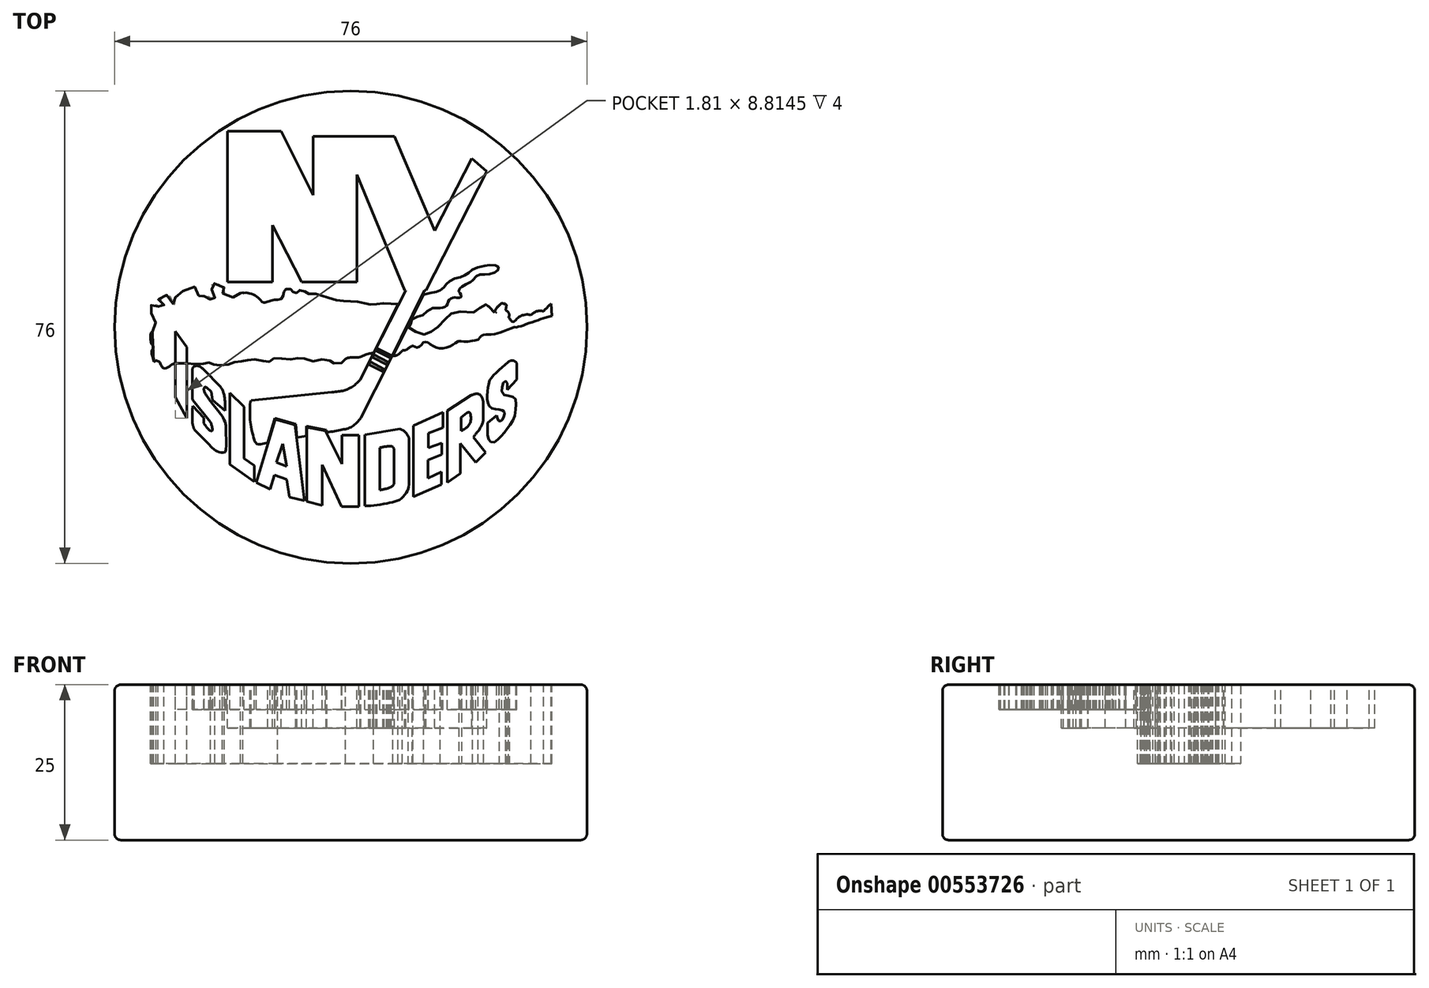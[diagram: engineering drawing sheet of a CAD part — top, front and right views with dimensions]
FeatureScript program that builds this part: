
annotation { "Feature Type Name" : "Feature", "Feature Type Description" : "" }
export const myFeature = defineFeature(function(context is Context, id is Id, definition is map)
    precondition{}
    {
        {
            var Q0;
            Q0=qCreatedBy(makeId("Top.planeOp"),FACE);
            var sketch = newSketch(context, id + "F0", { "sketchPlane" : qUnion([Q0])});
            skCircle(sketch, "E0", {"center": v(0, -1.1) * mm, "radius": 38 * mm});
            skLineSegment(sketch, "E1", {"start": v(0, 69.03) * mm, "end": v(0, -71.76) * mm, "construction": true});
            skLineSegment(sketch, "E2", {"start": v(-75.61, 0) * mm, "end": v(99.67, 0) * mm, "construction": true});
            skSolve(sketch);
        }
        {
            var Q0;
            Q0 = qSketchRegion(id + "F0", true);
            extrude(context, id + "F1", {"entities" : qUnion([Q0]), "depth" : 25 * mm, "offsetDistance" : 25 * mm});
        }
        {
            var Q0;
            Q0=makeQuery(id+"F1.opExtrude","CAP_FACE",FACE,{"disambiguationData":[OSD([sQuery(id+"F0.wireOp",EDGE,"E0")])],"isStart":false});
            var sketch = newSketch(context, id + "F2", { "sketchPlane" : qUnion([Q0])});
            skLineSegment(sketch, "E3", {"start": v(-35.12, 0) * mm, "end": v(34.88, 0) * mm, "construction": true});
            skLineSegment(sketch, "E4", {"start": v(-0.12, 35) * mm, "end": v(-0.12, -35) * mm, "construction": true});
            skFitSpline(sketch, "E5", {"points": [v(11.7, 4.15) * mm, v(12.74, 4.37) * mm, v(13.63, 4.59) * mm, v(14.2, 4.75) * mm, v(14.49, 4.87) * mm, v(14.91, 5.19) * mm, v(15.25, 5.66) * mm, v(15.5, 5.95) * mm, v(15.74, 6.16) * mm, v(16.14, 6.45) * mm, v(17.03, 6.84) * mm, v(17.65, 6.97) * mm, v(18.13, 7.13) * mm, v(18.63, 7.48) * mm, v(19.04, 7.7) * mm, v(19.46, 8.1) * mm, v(19.77, 8.33) * mm, v(21.3, 8.7) * mm, v(21.78, 8.8) * mm, v(22.45, 8.88) * mm, v(23.2, 8.86) * mm, v(23.6, 8.72) * mm, v(23.78, 8.58) * mm, v(23.82, 8.4) * mm, v(23.7, 8.11) * mm, v(23.48, 7.92) * mm, v(23.04, 7.63) * mm, v(22.45, 7.44) * mm, v(21.78, 7.39) * mm, v(21.36, 7.4) * mm, v(20.84, 7.4) * mm, v(20.5, 7.28) * mm, v(20.19, 7.05) * mm, v(19.63, 6.42) * mm], "startDerivative": vector(24.71, 4.93) * mm, "endDerivative": vector(-15.7, -18.75) * mm});
            skFitSpline(sketch, "E6", {"points": [v(19.63, 6.42) * mm, v(19.32, 6.22) * mm, v(18.96, 6.04) * mm, v(18.65, 5.87) * mm, v(18.35, 5.71) * mm, v(18.1, 5.56) * mm, v(17.82, 5.35) * mm, v(17.6, 5.17) * mm, v(17.5, 5.01) * mm, v(17.42, 4.92) * mm, v(17.36, 4.73) * mm, v(17.38, 4.6) * mm, v(17.62, 4.34) * mm, v(17.77, 4.07) * mm, v(17.79, 3.85) * mm, v(17.66, 3.7) * mm, v(17.42, 3.62) * mm, v(17.09, 3.65) * mm, v(16.9, 3.71) * mm, v(16.72, 3.72) * mm, v(16.47, 3.67) * mm, v(16.23, 3.58) * mm, v(16.09, 3.5) * mm, v(15.85, 3.3) * mm, v(15.7, 3.1) * mm, v(15.64, 2.87) * mm, v(15.55, 2.58) * mm, v(15.44, 2.41) * mm, v(15.27, 2.24) * mm, v(15.04, 2.12) * mm, v(14.7, 2.01) * mm, v(14.41, 2) * mm], "startDerivative": vector(-7.8, -5.36) * mm, "endDerivative": vector(-8.37, 0.32) * mm});
            skFitSpline(sketch, "E7", {"points": [v(14.41, 2) * mm, v(13.84, 2) * mm, v(13.39, 2) * mm, v(13.15, 1.97) * mm, v(12.9, 1.87) * mm, v(12.56, 1.72) * mm, v(12.29, 1.49) * mm, v(12.05, 1.25) * mm, v(11.85, 1) * mm, v(11.68, 0.85) * mm, v(11.52, 0.74) * mm, v(11.27, 0.7) * mm, v(10.98, 0.66) * mm, v(10.63, 0.6) * mm, v(10.3, 0.47) * mm, v(10.03, 0.34) * mm, v(9.87, 0.2) * mm, v(9.82, -0.1) * mm, v(9.85, -0.3) * mm, v(9.7, -0.57) * mm, v(9.56, -0.74) * mm, v(9.37, -0.82) * mm, v(9.23, -0.85) * mm, v(9.16, -0.94) * mm, v(9.27, -1.08) * mm, v(9.63, -1.38) * mm, v(10.17, -1.66) * mm, v(10.63, -1.9) * mm, v(11.32, -2.17) * mm, v(11.8, -2.26) * mm, v(12.26, -2.18) * mm, v(12.67, -2) * mm, v(13.18, -1.71) * mm, v(13.63, -1.38) * mm, v(14, -1.08) * mm, v(14.58, -0.5) * mm, v(15.24, 0.2) * mm, v(15.7, 0.68) * mm, v(16, 0.98) * mm, v(16.33, 1.22) * mm, v(16.62, 1.37) * mm, v(18.1, 1.38) * mm, v(19.53, 1.32) * mm, v(20.02, 1.3) * mm, v(20.4, 1.61) * mm, v(20.8, 2.01) * mm, v(21.28, 2.45) * mm, v(21.53, 2.55) * mm, v(21.76, 2.58) * mm, v(22.07, 2.5) * mm, v(22.26, 2.41) * mm, v(22.37, 2.2) * mm, v(22.5, 1.9) * mm, v(22.65, 1.62) * mm, v(22.78, 1.48) * mm, v(23.09, 1.31) * mm, v(23.33, 1.26) * mm, v(23.42, 1.48) * mm, v(23.48, 2.06) * mm, v(23.73, 2.46) * mm, v(24.06, 2.7) * mm, v(24.43, 2.83) * mm, v(24.7, 2.89) * mm, v(24.9, 2.76) * mm, v(25.02, 2.58) * mm, v(25.01, 2.18) * mm, v(24.98, 1.94) * mm, v(24.9, 1.74) * mm, v(24.94, 1.64) * mm], "startDerivative": vector(-31.94, -0.17) * mm, "endDerivative": vector(9.21, -12.06) * mm});
            skFitSpline(sketch, "E8", {"points": [v(24.94, 1.64) * mm, v(25.2, 1.45) * mm, v(25.4, 1.24) * mm, v(25.52, 0.97) * mm, v(25.53, 0.77) * mm, v(25.48, 0.67) * mm, v(25.38, 0.57) * mm], "startDerivative": vector(1.37, -0.88) * mm, "endDerivative": vector(-0.79, -0.78) * mm});
            skFitSpline(sketch, "E9", {"points": [v(25.38, 0.57) * mm, v(25.5, 0.39) * mm, v(25.69, 0.1) * mm, v(25.84, -0.09) * mm, v(26.05, -0.21) * mm, v(26.34, -0.13) * mm, v(26.63, 0.17) * mm, v(27.02, 0.53) * mm, v(27.47, 0.77) * mm, v(27.77, 0.86) * mm, v(28.33, 0.94) * mm, v(28.7, 0.92) * mm, v(29, 0.84) * mm], "startDerivative": vector(1.82, -2.56) * mm, "endDerivative": vector(3.86, -1.18) * mm});
            skFitSpline(sketch, "E10", {"points": [v(29, 0.84) * mm, v(29.37, 1.19) * mm, v(29.95, 1.47) * mm, v(30.43, 1.52) * mm, v(30.83, 1.5) * mm, v(31, 1.44) * mm], "startDerivative": vector(1.54, 1.64) * mm, "endDerivative": vector(1.18, -0.49) * mm});
            skFitSpline(sketch, "E11", {"points": [v(31, 1.44) * mm, v(31.52, 2) * mm, v(31.91, 2.41) * mm, v(32.22, 2.7) * mm], "startDerivative": vector(1.39, 1.48) * mm, "endDerivative": vector(1.07, 0.93) * mm});
            skLineSegment(sketch, "E12", {"start": v(32.22, 2.7) * mm, "end": v(32.34, 0.68) * mm});
            skFitSpline(sketch, "E13", {"points": [v(32.34, 0.68) * mm, v(30.83, 0.3) * mm, v(30.27, 0.09) * mm, v(29.6, -0.15) * mm, v(28.8, -0.43) * mm, v(27.96, -0.73) * mm, v(27.5, -0.88) * mm, v(26.9, -1.05) * mm, v(26.54, -1.1) * mm, v(26.27, -1.1) * mm, v(24.87, -1.65) * mm, v(23.98, -1.97) * mm, v(23.24, -2.2) * mm, v(22.38, -2.26) * mm, v(21.83, -2.3) * mm, v(21.39, -2.34) * mm], "startDerivative": vector(-17.48, -4.1) * mm, "endDerivative": vector(-8.33, -0.85) * mm});
            skFitSpline(sketch, "E14", {"points": [v(21.39, -2.34) * mm, v(21.19, -2.4) * mm, v(20.98, -2.53) * mm, v(20.83, -2.67) * mm, v(20.73, -2.81) * mm, v(20.6, -3) * mm, v(20.5, -3.07) * mm], "startDerivative": vector(-1.15, -0.25) * mm, "endDerivative": vector(-0.8, -0.43) * mm});
            skFitSpline(sketch, "E15", {"points": [v(20.5, -3.07) * mm, v(19.95, -3.22) * mm, v(19.36, -3.32) * mm, v(18.4, -3.43) * mm, v(17.85, -3.37) * mm, v(17.4, -3.35) * mm, v(16.85, -3.62) * mm, v(16.44, -3.93) * mm, v(15.92, -4.18) * mm, v(15.16, -4.44) * mm, v(14.41, -4.48) * mm, v(13.87, -4.4) * mm, v(13.3, -4.14) * mm, v(12.8, -3.84) * mm, v(12.36, -3.52) * mm, v(12.04, -3.45) * mm, v(11.7, -3.53) * mm, v(11.42, -3.85) * mm, v(11.12, -4.16) * mm, v(10.74, -4.37) * mm, v(10.49, -4.3) * mm, v(10.22, -4.17) * mm, v(10.03, -4.1) * mm], "startDerivative": vector(-11.38, -3.46) * mm, "endDerivative": vector(-6.3, 2.42) * mm});
            skFitSpline(sketch, "E16", {"points": [v(10.03, -4.1) * mm, v(9.92, -4.1) * mm, v(9.65, -4.22) * mm, v(9.32, -4.43) * mm, v(8.89, -4.73) * mm, v(8.6, -4.82) * mm, v(8.32, -4.82) * mm], "startDerivative": vector(-0.98, 0.14) * mm, "endDerivative": vector(-1.78, 0.03) * mm});
            skFitSpline(sketch, "E17", {"points": [v(8.32, -4.82) * mm, v(8.15, -5.04) * mm, v(7.88, -5.27) * mm, v(7.43, -5.6) * mm, v(6.93, -5.7) * mm, v(6.76, -5.7) * mm], "startDerivative": vector(-0.93, -1.24) * mm, "endDerivative": vector(-1.05, 0.05) * mm});
            skLineSegment(sketch, "E18", {"start": v(6.76, -5.7) * mm, "end": v(11.7, 4.15) * mm});
            skFitSpline(sketch, "E19", {"points": [v(7.58, 2.6) * mm, v(6.67, 2.7) * mm, v(5.54, 2.78) * mm, v(4.48, 2.7) * mm, v(3.9, 2.58) * mm, v(3.07, 2.55) * mm, v(2.5, 2.7) * mm, v(1.46, 2.93) * mm, v(0.59, 3.04) * mm, v(-0.44, 3.1) * mm, v(-1.4, 3.12) * mm, v(-2.45, 3.3) * mm, v(-3.72, 3.65) * mm, v(-4.8, 4.04) * mm, v(-5.33, 4.22) * mm, v(-6.14, 4.3) * mm, v(-7, 4.28) * mm, v(-7.27, 4.55) * mm, v(-7.86, 4.83) * mm, v(-8.24, 4.84) * mm, v(-8.56, 4.55) * mm, v(-8.73, 4.42) * mm, v(-9, 4.44) * mm, v(-9.2, 4.55) * mm, v(-9.4, 4.77) * mm, v(-9.56, 5) * mm, v(-9.99, 5.12) * mm, v(-10.36, 5.06) * mm, v(-10.57, 4.92) * mm, v(-10.73, 4.68) * mm, v(-10.83, 4.46) * mm, v(-10.86, 4.09) * mm, v(-10.9, 3.8) * mm, v(-11.04, 3.6) * mm, v(-11.3, 3.4) * mm, v(-11.49, 3.33) * mm, v(-11.76, 3.34) * mm], "startDerivative": vector(-24.6, 2.23) * mm, "endDerivative": vector(-14.82, 1.29) * mm});
            skFitSpline(sketch, "E20", {"points": [v(-11.76, 3.34) * mm, v(-12.17, 3.33) * mm, v(-12.51, 3.25) * mm, v(-12.75, 3.19) * mm, v(-13.02, 3.12) * mm, v(-13.25, 3.04) * mm, v(-13.5, 2.96) * mm, v(-13.68, 2.91) * mm, v(-13.93, 2.86) * mm, v(-14.37, 3.07) * mm, v(-14.65, 3.4) * mm, v(-14.95, 3.7) * mm, v(-15.35, 3.97) * mm, v(-15.8, 4.18) * mm, v(-16.32, 4.37) * mm, v(-16.84, 4.44) * mm, v(-17.34, 4.43) * mm, v(-17.36, 4.46) * mm], "startDerivative": vector(-6.43, 0.22) * mm, "endDerivative": vector(-0.34, 2.1) * mm});
            skFitSpline(sketch, "E21", {"points": [v(-17.36, 4.46) * mm, v(-17.72, 4.38) * mm], "startDerivative": vector(-0.36, -0.09) * mm, "endDerivative": vector(-0.36, -0.09) * mm});
            skFitSpline(sketch, "E22", {"points": [v(-17.72, 4.38) * mm, v(-17.99, 4.31) * mm, v(-18.27, 4.12) * mm, v(-18.48, 3.87) * mm, v(-18.67, 3.62) * mm, v(-18.87, 3.66) * mm, v(-19.13, 3.81) * mm, v(-19.53, 4.05) * mm, v(-19.93, 4.15) * mm, v(-20.3, 4.25) * mm, v(-20.6, 4.3) * mm, v(-20.66, 4.38) * mm, v(-20.7, 4.44) * mm, v(-20.65, 4.51) * mm, v(-20.5, 4.64) * mm, v(-20.39, 4.82) * mm, v(-20.32, 5.04) * mm, v(-20.34, 5.21) * mm, v(-20.47, 5.4) * mm, v(-20.78, 5.6) * mm, v(-21.05, 5.73) * mm, v(-21.43, 5.85) * mm, v(-21.88, 5.91) * mm, v(-22.31, 5.96) * mm, v(-22.45, 5.92) * mm, v(-22.52, 5.83) * mm, v(-22.54, 5.56) * mm, v(-22.47, 5.2) * mm, v(-22.35, 4.92) * mm, v(-22.23, 4.57) * mm, v(-22.14, 4.33) * mm, v(-22.1, 4.12) * mm, v(-22.04, 3.85) * mm, v(-21.9, 3.67) * mm, v(-21.84, 3.62) * mm, v(-21.85, 3.54) * mm, v(-21.91, 3.42) * mm, v(-22.02, 3.27) * mm, v(-22.2, 3.18) * mm, v(-22.38, 3.16) * mm, v(-22.55, 3.26) * mm, v(-22.67, 3.43) * mm, v(-22.81, 3.75) * mm, v(-22.98, 3.96) * mm, v(-23.11, 4.06) * mm, v(-23.25, 4.08) * mm, v(-23.44, 4.04) * mm, v(-23.59, 3.9) * mm, v(-23.72, 3.78) * mm, v(-23.84, 3.65) * mm, v(-23.97, 3.58) * mm, v(-24.16, 3.55) * mm, v(-24.3, 3.63) * mm, v(-24.4, 3.77) * mm, v(-24.49, 4.07) * mm, v(-24.56, 4.6) * mm, v(-24.6, 4.98) * mm, v(-24.78, 5.32) * mm, v(-24.97, 5.4) * mm, v(-25.33, 5.34) * mm, v(-25.7, 5.18) * mm, v(-26.05, 5.02) * mm, v(-26.7, 4.77) * mm, v(-27.11, 4.67) * mm, v(-27.5, 4.49) * mm, v(-27.73, 4.38) * mm, v(-28.01, 4.06) * mm, v(-28.17, 3.83) * mm, v(-28.24, 3.6) * mm, v(-28.24, 3.32) * mm, v(-28.27, 2.87) * mm, v(-28.32, 2.57) * mm, v(-28.5, 2.51) * mm, v(-28.62, 2.69) * mm, v(-28.74, 3.04) * mm, v(-28.85, 3.47) * mm, v(-29, 3.78) * mm, v(-29.24, 4) * mm, v(-29.8, 4.07) * mm, v(-30.12, 4.06) * mm, v(-30.65, 3.86) * mm, v(-30.9, 3.68) * mm, v(-30.98, 3.51) * mm, v(-30.9, 3.18) * mm, v(-30.77, 2.97) * mm, v(-30.5, 2.83) * mm, v(-30.29, 2.78) * mm, v(-30.1, 2.67) * mm, v(-30.03, 2.57) * mm, v(-30.06, 2.36) * mm, v(-30.23, 2.14) * mm, v(-30.39, 1.95) * mm, v(-30.55, 1.81) * mm, v(-30.72, 1.95) * mm, v(-30.88, 2.14) * mm, v(-31.09, 2.36) * mm, v(-31.23, 2.45) * mm, v(-31.42, 2.54) * mm, v(-31.64, 2.62) * mm, v(-31.85, 2.61) * mm, v(-32.04, 2.53) * mm, v(-32.16, 2.3) * mm, v(-32.17, 2.14) * mm, v(-32.08, 1.95) * mm, v(-31.97, 1.73) * mm, v(-31.95, 1.6) * mm, v(-32.03, 1.43) * mm, v(-32.07, 0.96) * mm, v(-32, 0.67) * mm, v(-31.8, 0.46) * mm, v(-31.56, 0.18) * mm, v(-31.44, -0.14) * mm, v(-31.32, -0.65) * mm, v(-31.35, -1.15) * mm, v(-31.4, -1.57) * mm, v(-31.65, -1.7) * mm, v(-31.85, -1.78) * mm, v(-32.03, -1.9) * mm, v(-32.18, -2.05) * mm, v(-32.1, -3.78) * mm, v(-31.9, -3.9) * mm, v(-31.77, -4.33) * mm, v(-31.77, -4.6) * mm, v(-31.99, -4.77) * mm, v(-31.68, -6.65) * mm], "startDerivative": vector(-33.91, -4.92) * mm, "endDerivative": vector(32.77, -115.7) * mm});
            skFitSpline(sketch, "E23", {"points": [v(-31.68, -6.65) * mm, v(-31.47, -6.51) * mm, v(-31.27, -6.47) * mm, v(-31, -6.54) * mm, v(-30.74, -6.73) * mm, v(-30.6, -6.99) * mm, v(-30.44, -7.36) * mm, v(-30.25, -7.6) * mm, v(-29.92, -7.71) * mm, v(-29.34, -7.5) * mm, v(-28.77, -7.1) * mm, v(-28.5, -6.94) * mm, v(-28.28, -6.87) * mm, v(-28.24, -6.87) * mm], "startDerivative": vector(2.98, 2.23) * mm, "endDerivative": vector(1.17, -0.17) * mm});
            skLineSegment(sketch, "E24", {"start": v(-28.24, -6.87) * mm, "end": v(-28.24, -1.76) * mm});
            skLineSegment(sketch, "E25", {"start": v(-28.24, -1.76) * mm, "end": v(-26.35, -4.3) * mm});
            skLineSegment(sketch, "E26", {"start": v(-26.35, -4.3) * mm, "end": v(-26.35, -6.93) * mm});
            skFitSpline(sketch, "E27", {"points": [v(-26.35, -6.93) * mm, v(-25.82, -7.02) * mm, v(-25.19, -7.05) * mm, v(-24.3, -7.07) * mm, v(-23.82, -6.99) * mm, v(-23.4, -6.87) * mm, v(-23.12, -6.83) * mm, v(-22.9, -6.8) * mm, v(-22.7, -6.86) * mm, v(-22.5, -6.98) * mm, v(-22.1, -7.1) * mm, v(-22.03, -7.1) * mm, v(-21.61, -7.2) * mm, v(-21.55, -7.2) * mm, v(-21.03, -7.25) * mm, v(-20.36, -7.21) * mm, v(-19.72, -7.12) * mm, v(-19.2, -6.93) * mm, v(-18.86, -6.77) * mm, v(-18.34, -6.7) * mm, v(-17.8, -6.6) * mm, v(-17.74, -6.6) * mm, v(-17.11, -6.6) * mm, v(-16.83, -6.5) * mm, v(-16.76, -6.5) * mm, v(-16.35, -6.32) * mm, v(-16.28, -6.32) * mm, v(-15.68, -6.27) * mm, v(-15.04, -6.28) * mm, v(-14.39, -6.42) * mm, v(-13.7, -6.66) * mm, v(-13.29, -6.72) * mm, v(-13.2, -6.7) * mm, v(-12.88, -6.57) * mm, v(-12.57, -6.35) * mm, v(-12.35, -6.13) * mm, v(-11.87, -6.06) * mm, v(-11.17, -6.13) * mm, v(-11.1, -6.13) * mm, v(-10.3, -6.28) * mm, v(-9.57, -6.28) * mm, v(-9.5, -6.28) * mm, v(-8.87, -6.21) * mm, v(-8.45, -6.03) * mm, v(-8.39, -6.03) * mm, v(-7.8, -6.09) * mm, v(-7.1, -6.3) * mm, v(-6.37, -6.54) * mm, v(-5.44, -6.48) * mm, v(-4.89, -6.3) * mm, v(-4.12, -6.18) * mm, v(-3.53, -6.35) * mm, v(-3.25, -6.64) * mm, v(-3.17, -6.64) * mm, v(-2.98, -6.83) * mm, v(-2.54, -6.93) * mm, v(-2.1, -6.93) * mm, v(-1.47, -6.86) * mm, v(-1.05, -6.62) * mm, v(-0.96, -6.49) * mm, v(-0.84, -6.2) * mm], "startDerivative": vector(27.49, -5.87) * mm, "endDerivative": vector(9.48, 21.77) * mm});
            skFitSpline(sketch, "E28", {"points": [v(-0.84, -6.2) * mm, v(-0.52, -6.05) * mm, v(0.3, -5.96) * mm, v(1.29, -5.94) * mm, v(2.31, -5.56) * mm, v(3.24, -5.28) * mm, v(3.67, -5.24) * mm], "startDerivative": vector(2.4, 1.4) * mm, "endDerivative": vector(3.07, 0.18) * mm});
            skLineSegment(sketch, "E29", {"start": v(3.67, -5.24) * mm, "end": v(7.58, 2.6) * mm});
            skSolve(sketch);
        }
        {
            var Q0;
            Q0 = qSketchRegion(id + "F2", true);
            extrude(context, id + "F3", {"entities" : qUnion([Q0]), "operationType" : NewBodyOperationType.REMOVE, "oppositeDirection" : true, "depth" : 12.7 * mm, "offsetDistance" : 25 * mm});
        }
        {
            var Q0;
            Q0=makeQuery(id+"F2.imprint","IMPRINT",FACE,{"disambiguationData":[TD([[makeQuery(id+"F2.imprint","IMPRINT",EDGE,{"derivedFrom":sQuery(id+"F2.wireOp",EDGE,"E5")}),1.0]])]});
            var sketch = newSketch(context, id + "F4", { "sketchPlane" : qUnion([Q0])});
            skLineSegment(sketch, "E30", {"start": v(-28.2, -6.92) * mm, "end": v(-28.2, -12.34) * mm});
            skLineSegment(sketch, "E31", {"start": v(-28.2, -12.34) * mm, "end": v(-26.39, -15.74) * mm});
            skLineSegment(sketch, "E32", {"start": v(-26.39, -15.74) * mm, "end": v(-26.39, -6.92) * mm});
            skLineSegment(sketch, "E33", {"start": v(-26.39, -6.92) * mm, "end": v(-28.2, -6.92) * mm});
            skLineSegment(sketch, "E34", {"start": v(-25.44, -13.74) * mm, "end": v(-23.66, -15.64) * mm});
            skLineSegment(sketch, "E35", {"start": v(-23.66, -15.64) * mm, "end": v(-23.63, -16.56) * mm});
            skFitSpline(sketch, "E36", {"points": [v(-23.63, -16.56) * mm, v(-23.25, -17.1) * mm, v(-22.94, -17.49) * mm, v(-22.72, -17.68) * mm, v(-22.54, -17.8) * mm, v(-22.38, -17.77) * mm, v(-22.27, -17.72) * mm, v(-22.25, -17.54) * mm, v(-22.33, -17.08) * mm, v(-22.44, -16.67) * mm, v(-22.54, -16.36) * mm], "startDerivative": vector(2.6, -3.9) * mm, "endDerivative": vector(-0.95, 2.9) * mm});
            skLineSegment(sketch, "E37", {"start": v(-22.54, -16.36) * mm, "end": v(-25.4, -12.83) * mm});
            skFitSpline(sketch, "E38", {"points": [v(-25.4, -12.83) * mm, v(-25.5, -12.55) * mm], "startDerivative": vector(-0.1, 0.28) * mm, "endDerivative": vector(-0.1, 0.28) * mm});
            skLineSegment(sketch, "E39", {"start": v(-25.5, -12.55) * mm, "end": v(-25.5, -7.87) * mm});
            skFitSpline(sketch, "E40", {"points": [v(-25.5, -7.87) * mm, v(-25.41, -7.66) * mm, v(-25.2, -7.42) * mm, v(-24.88, -7.31) * mm, v(-24.56, -7.32) * mm, v(-24.11, -7.5) * mm, v(-24.05, -7.54) * mm, v(-23.58, -8) * mm], "startDerivative": vector(0.57, 1.7) * mm, "endDerivative": vector(2.97, -2.83) * mm});
            skLineSegment(sketch, "E41", {"start": v(-23.58, -8) * mm, "end": v(-21.04, -10.56) * mm});
            skFitSpline(sketch, "E42", {"points": [v(-21.04, -10.56) * mm, v(-20.82, -10.88) * mm, v(-20.6, -11.3) * mm, v(-20.48, -11.66) * mm, v(-20.34, -12.21) * mm, v(-20.25, -12.85) * mm, v(-20.23, -13.23) * mm, v(-20.22, -14.01) * mm, v(-20.24, -14.53) * mm], "startDerivative": vector(1.88, -2.82) * mm, "endDerivative": vector(-0.2, -3.71) * mm});
            skLineSegment(sketch, "E43", {"start": v(-20.24, -14.53) * mm, "end": v(-22.26, -12.82) * mm});
            skLineSegment(sketch, "E44", {"start": v(-22.26, -12.82) * mm, "end": v(-22.43, -11.5) * mm});
            skFitSpline(sketch, "E45", {"points": [v(-22.43, -11.5) * mm, v(-22.74, -11.17) * mm, v(-23.07, -10.9) * mm, v(-23.29, -10.75) * mm, v(-23.46, -10.74) * mm, v(-23.58, -10.84) * mm, v(-23.62, -11.05) * mm, v(-23.58, -11.35) * mm, v(-23.44, -11.7) * mm, v(-23.12, -12.2) * mm, v(-22.79, -12.66) * mm], "startDerivative": vector(-2.6, 2.8) * mm, "endDerivative": vector(2.54, -3.46) * mm});
            skLineSegment(sketch, "E46", {"start": v(-22.79, -12.66) * mm, "end": v(-20.68, -15.39) * mm});
            skFitSpline(sketch, "E47", {"points": [v(-20.68, -15.39) * mm, v(-20.41, -15.94) * mm, v(-20.18, -16.48) * mm, v(-20.11, -17.05) * mm, v(-20.1, -17.84) * mm, v(-20.14, -21.03) * mm, v(-20.55, -21.26) * mm, v(-21.07, -21.22) * mm, v(-21.68, -20.96) * mm, v(-22.03, -20.71) * mm, v(-25.14, -17.58) * mm], "startDerivative": vector(3.44, -7.02) * mm, "endDerivative": vector(-18.63, 19.24) * mm});
            skFitSpline(sketch, "E48", {"points": [v(-25.14, -17.58) * mm, v(-25.37, -16.99) * mm, v(-25.47, -16.45) * mm, v(-25.44, -13.74) * mm], "startDerivative": vector(-1.05, 2.48) * mm, "endDerivative": vector(0.19, 6.28) * mm});
            skLineSegment(sketch, "E49", {"start": v(-19.43, -11.65) * mm, "end": v(-17.19, -13.87) * mm});
            skLineSegment(sketch, "E50", {"start": v(-17.19, -13.87) * mm, "end": v(-17.19, -22.19) * mm});
            skLineSegment(sketch, "E51", {"start": v(-17.19, -22.19) * mm, "end": v(-15.5, -23.34) * mm});
            skLineSegment(sketch, "E52", {"start": v(-15.5, -23.34) * mm, "end": v(-15.5, -25.93) * mm});
            skLineSegment(sketch, "E53", {"start": v(-15.5, -25.93) * mm, "end": v(-19.45, -23.16) * mm});
            skLineSegment(sketch, "E54", {"start": v(-19.45, -23.16) * mm, "end": v(-19.43, -11.65) * mm});
            skLineSegment(sketch, "E55", {"start": v(-11.94, -22.87) * mm, "end": v(-10.32, -23.45) * mm});
            skLineSegment(sketch, "E56", {"start": v(-10.32, -23.45) * mm, "end": v(-10.95, -19.87) * mm});
            skLineSegment(sketch, "E57", {"start": v(-10.95, -19.87) * mm, "end": v(-11.94, -22.87) * mm});
            skLineSegment(sketch, "E58", {"start": v(-15.2, -26.06) * mm, "end": v(-12.95, -27.16) * mm});
            skLineSegment(sketch, "E59", {"start": v(-12.95, -27.16) * mm, "end": v(-12.25, -24.86) * mm});
            skLineSegment(sketch, "E60", {"start": v(-12.25, -24.86) * mm, "end": v(-10.33, -25.58) * mm});
            skLineSegment(sketch, "E61", {"start": v(-10.33, -25.58) * mm, "end": v(-9.84, -28.42) * mm});
            skLineSegment(sketch, "E62", {"start": v(-9.84, -28.42) * mm, "end": v(-7.44, -29.01) * mm});
            skLineSegment(sketch, "E63", {"start": v(-7.44, -29.01) * mm, "end": v(-8.97, -16.78) * mm});
            skLineSegment(sketch, "E64", {"start": v(-8.97, -16.78) * mm, "end": v(-12.18, -15.9) * mm});
            skLineSegment(sketch, "E65", {"start": v(-12.18, -15.9) * mm, "end": v(-15.2, -26.06) * mm});
            skLineSegment(sketch, "E66", {"start": v(-7.08, -29.13) * mm, "end": v(-4.58, -29.74) * mm});
            skLineSegment(sketch, "E67", {"start": v(-4.58, -29.74) * mm, "end": v(-4.58, -23.24) * mm});
            skLineSegment(sketch, "E68", {"start": v(-4.58, -23.24) * mm, "end": v(-1.47, -29.95) * mm});
            skLineSegment(sketch, "E69", {"start": v(-1.47, -29.95) * mm, "end": v(1.33, -29.95) * mm});
            skLineSegment(sketch, "E70", {"start": v(1.33, -29.95) * mm, "end": v(1.33, -18.46) * mm});
            skLineSegment(sketch, "E71", {"start": v(1.33, -18.46) * mm, "end": v(-1.42, -18.46) * mm});
            skLineSegment(sketch, "E72", {"start": v(-1.42, -18.46) * mm, "end": v(-1.42, -23.12) * mm});
            skLineSegment(sketch, "E73", {"start": v(-1.42, -23.12) * mm, "end": v(-4.07, -17.77) * mm});
            skLineSegment(sketch, "E74", {"start": v(-4.07, -17.77) * mm, "end": v(-7.09, -17.17) * mm});
            skLineSegment(sketch, "E75", {"start": v(-7.09, -17.17) * mm, "end": v(-7.08, -29.13) * mm});
            skLineSegment(sketch, "E76", {"start": v(2.29, -18.4) * mm, "end": v(2.29, -29.84) * mm});
            skFitSpline(sketch, "E77", {"points": [v(2.29, -29.84) * mm, v(3.59, -29.77) * mm, v(5.3, -29.54) * mm, v(6.65, -29.26) * mm, v(7.6, -28.99) * mm, v(8.35, -28.45) * mm, v(8.93, -27.74) * mm, v(9.23, -27.1) * mm, v(9.35, -26.34) * mm, v(9.35, -25) * mm], "startDerivative": vector(10.25, 0.4) * mm, "endDerivative": vector(-0.34, 11.63) * mm});
            skFitSpline(sketch, "E78", {"points": [v(9.35, -25) * mm, v(9.35, -18.92) * mm], "startDerivative": vector(0, 6.08) * mm, "endDerivative": vector(0, 6.08) * mm});
            skFitSpline(sketch, "E79", {"points": [v(9.35, -18.92) * mm, v(9.05, -18.3) * mm, v(8.45, -17.73) * mm, v(7.92, -17.47) * mm], "startDerivative": vector(-0.71, 1.87) * mm, "endDerivative": vector(-1.68, 0.67) * mm});
            skLineSegment(sketch, "E80", {"start": v(2.29, -18.4) * mm, "end": v(7.92, -17.47) * mm});
            skLineSegment(sketch, "E81", {"start": v(4.69, -27.28) * mm, "end": v(4.69, -20.48) * mm});
            skFitSpline(sketch, "E82", {"points": [v(4.69, -20.48) * mm, v(5.58, -20.3) * mm, v(6.14, -20.25) * mm, v(6.57, -20.23) * mm, v(6.79, -20.37) * mm, v(6.93, -20.6) * mm], "startDerivative": vector(3.36, 0.82) * mm, "endDerivative": vector(0.83, -1.63) * mm});
            skLineSegment(sketch, "E83", {"start": v(6.93, -20.6) * mm, "end": v(6.93, -26.32) * mm});
            skFitSpline(sketch, "E84", {"points": [v(6.93, -26.32) * mm, v(6.72, -26.65) * mm, v(6.14, -26.95) * mm, v(5.4, -27.15) * mm, v(4.69, -27.28) * mm], "startDerivative": vector(-0.77, -1.78) * mm, "endDerivative": vector(-2.65, -0.42) * mm});
            skLineSegment(sketch, "E85", {"start": v(10.08, -16.94) * mm, "end": v(10.08, -28.36) * mm});
            skLineSegment(sketch, "E86", {"start": v(10.08, -28.36) * mm, "end": v(14.58, -26.37) * mm});
            skLineSegment(sketch, "E87", {"start": v(14.58, -26.37) * mm, "end": v(14.58, -24.36) * mm});
            skLineSegment(sketch, "E88", {"start": v(14.58, -24.36) * mm, "end": v(12.41, -25.37) * mm});
            skLineSegment(sketch, "E89", {"start": v(12.41, -25.37) * mm, "end": v(12.41, -22.49) * mm});
            skLineSegment(sketch, "E90", {"start": v(12.41, -22.49) * mm, "end": v(14.64, -21.55) * mm});
            skLineSegment(sketch, "E91", {"start": v(14.64, -21.55) * mm, "end": v(14.64, -19.7) * mm});
            skLineSegment(sketch, "E92", {"start": v(14.64, -19.7) * mm, "end": v(12.46, -20.47) * mm});
            skLineSegment(sketch, "E93", {"start": v(12.46, -20.47) * mm, "end": v(12.46, -18.15) * mm});
            skLineSegment(sketch, "E94", {"start": v(12.46, -18.15) * mm, "end": v(14.85, -17.26) * mm});
            skLineSegment(sketch, "E95", {"start": v(14.85, -17.26) * mm, "end": v(14.85, -14.8) * mm});
            skLineSegment(sketch, "E96", {"start": v(14.85, -14.8) * mm, "end": v(10.08, -16.94) * mm});
            skLineSegment(sketch, "E97", {"start": v(17.62, -24.65) * mm, "end": v(17.62, -19.77) * mm});
            skLineSegment(sketch, "E98", {"start": v(17.62, -19.77) * mm, "end": v(20.08, -22.84) * mm});
            skLineSegment(sketch, "E99", {"start": v(20.08, -22.84) * mm, "end": v(21.7, -21.28) * mm});
            skLineSegment(sketch, "E100", {"start": v(21.7, -21.28) * mm, "end": v(19.74, -18.76) * mm});
            skLineSegment(sketch, "E101", {"start": v(17.62, -24.65) * mm, "end": v(15.56, -26.06) * mm});
            skLineSegment(sketch, "E102", {"start": v(15.56, -26.06) * mm, "end": v(15.56, -14.55) * mm});
            skLineSegment(sketch, "E103", {"start": v(15.56, -14.55) * mm, "end": v(19.35, -12.07) * mm});
            skFitSpline(sketch, "E104", {"points": [v(19.35, -12.07) * mm, v(19.75, -11.9) * mm, v(20.27, -11.8) * mm, v(20.68, -11.88) * mm, v(20.95, -12.12) * mm, v(21.13, -12.45) * mm, v(21.26, -12.84) * mm, v(21.32, -13.3) * mm], "startDerivative": vector(2.6, 1.38) * mm, "endDerivative": vector(0.22, -3.12) * mm});
            skLineSegment(sketch, "E105", {"start": v(21.32, -13.3) * mm, "end": v(21.32, -15.8) * mm});
            skFitSpline(sketch, "E106", {"points": [v(21.32, -15.8) * mm, v(21.27, -16.3) * mm, v(21.02, -16.93) * mm, v(20.75, -17.45) * mm, v(20.16, -18.23) * mm, v(19.74, -18.76) * mm], "startDerivative": vector(-0.05, -2.81) * mm, "endDerivative": vector(-1.9, -2.45) * mm});
            skLineSegment(sketch, "E107", {"start": v(17.74, -17.76) * mm, "end": v(17.74, -15.62) * mm});
            skLineSegment(sketch, "E108", {"start": v(17.74, -15.62) * mm, "end": v(18.67, -14.89) * mm});
            skFitSpline(sketch, "E109", {"points": [v(18.67, -14.89) * mm, v(18.82, -14.8) * mm, v(18.99, -14.78) * mm, v(19.2, -14.89) * mm, v(19.27, -15.11) * mm, v(19.34, -15.6) * mm, v(19.32, -16.02) * mm, v(19.27, -16.4) * mm, v(19, -16.83) * mm, v(18.72, -17.16) * mm, v(18.47, -17.35) * mm, v(18.14, -17.57) * mm, v(17.74, -17.76) * mm], "startDerivative": vector(2.38, 1.94) * mm, "endDerivative": vector(-4.32, -1.84) * mm});
            skLineSegment(sketch, "E110", {"start": v(23.5, -15.26) * mm, "end": v(21.99, -16.51) * mm});
            skLineSegment(sketch, "E111", {"start": v(21.99, -16.51) * mm, "end": v(21.99, -18.47) * mm});
            skFitSpline(sketch, "E112", {"points": [v(21.99, -18.47) * mm, v(22.1, -18.98) * mm, v(22.3, -19.3) * mm, v(22.46, -19.5) * mm, v(22.75, -19.62) * mm, v(23.18, -19.57) * mm, v(23.58, -19.26) * mm, v(23.9, -19) * mm, v(24.31, -18.51) * mm, v(24.79, -17.9) * mm, v(25.11, -17.45) * mm, v(25.5, -17) * mm, v(25.84, -16.49) * mm, v(26.18, -15.84) * mm, v(26.4, -15.23) * mm, v(26.57, -14.17) * mm, v(26.6, -13.56) * mm, v(26.54, -12.77) * mm, v(26.4, -12.44) * mm, v(26, -12.25) * mm, v(25.33, -12.11) * mm, v(24.85, -12.05) * mm, v(24.5, -11.84) * mm, v(24.3, -11.42) * mm, v(24.3, -10.95) * mm, v(24.45, -10.32) * mm, v(24.62, -9.95) * mm, v(24.82, -9.78) * mm, v(24.93, -9.78) * mm, v(25.03, -9.84) * mm, v(25.16, -10.05) * mm, v(25.2, -10.34) * mm, v(25.21, -10.68) * mm, v(25.2, -10.97) * mm, v(25.19, -11.19) * mm], "startDerivative": vector(2.82, -17.08) * mm, "endDerivative": vector(-1.15, -10.26) * mm});
            skLineSegment(sketch, "E113", {"start": v(25.19, -11.19) * mm, "end": v(26.74, -9.54) * mm});
            skLineSegment(sketch, "E114", {"start": v(26.74, -9.54) * mm, "end": v(26.74, -7.1) * mm});
            skFitSpline(sketch, "E115", {"points": [v(26.74, -7.1) * mm, v(26.69, -6.89) * mm, v(26.56, -6.7) * mm, v(26.31, -6.53) * mm, v(26.02, -6.44) * mm, v(25.65, -6.51) * mm, v(25.34, -6.7) * mm], "startDerivative": vector(-0.25, 1.47) * mm, "endDerivative": vector(-1.6, -1.12) * mm});
            skLineSegment(sketch, "E116", {"start": v(25.34, -6.7) * mm, "end": v(23.82, -7.96) * mm});
            skFitSpline(sketch, "E117", {"points": [v(23.82, -7.96) * mm, v(23.39, -8.4) * mm, v(22.98, -8.81) * mm, v(22.67, -9.2) * mm, v(22.44, -9.45) * mm, v(22.22, -10.03) * mm, v(22.12, -10.54) * mm, v(22.03, -11.1) * mm, v(21.97, -11.8) * mm, v(21.96, -12.51) * mm, v(22, -12.94) * mm, v(22.15, -13.48) * mm, v(22.4, -13.92) * mm, v(22.88, -14.25) * mm, v(23.4, -14.29) * mm, v(24, -14.34) * mm, v(24.42, -14.48) * mm, v(24.6, -14.6) * mm, v(24.68, -14.75) * mm, v(24.71, -14.95) * mm, v(24.7, -15.25) * mm, v(24.6, -15.55) * mm, v(24.42, -15.93) * mm, v(24.25, -16.1) * mm, v(24.11, -16.19) * mm, v(23.9, -16.18) * mm, v(23.7, -16.03) * mm, v(23.56, -15.57) * mm, v(23.5, -15.26) * mm], "startDerivative": vector(-9.9, -10.4) * mm, "endDerivative": vector(-1.66, 8.84) * mm});
            skSolve(sketch);
        }
        {
            var Q0;
            Q0 = qSketchRegion(id + "F4", true);
            extrude(context, id + "F5", {"entities" : qUnion([Q0]), "operationType" : NewBodyOperationType.REMOVE, "oppositeDirection" : true, "depth" : 4 * mm, "offsetDistance" : 25 * mm});
        }
        {
            var Q0;
            Q0=makeQuery(id+"F2.imprint","IMPRINT",FACE,{"disambiguationData":[TD([[makeQuery(id+"F2.imprint","IMPRINT",EDGE,{"derivedFrom":sQuery(id+"F2.wireOp",EDGE,"E5")}),1.0]])]});
            var sketch = newSketch(context, id + "F6", { "sketchPlane" : qUnion([Q0])});
            skLineSegment(sketch, "E118", {"start": v(-19.83, 6.2) * mm, "end": v(-12.59, 6.2) * mm});
            skLineSegment(sketch, "E119", {"start": v(-12.59, 6.2) * mm, "end": v(-12.59, 15.33) * mm});
            skLineSegment(sketch, "E120", {"start": v(-12.59, 15.33) * mm, "end": v(-7.89, 6.16) * mm});
            skLineSegment(sketch, "E121", {"start": v(-7.89, 6.16) * mm, "end": v(1, 6.16) * mm});
            skLineSegment(sketch, "E122", {"start": v(1, 6.16) * mm, "end": v(1, 23.45) * mm});
            skLineSegment(sketch, "E123", {"start": v(1, 23.45) * mm, "end": v(8.69, 4.87) * mm});
            skLineSegment(sketch, "E124", {"start": v(-19.83, 6.2) * mm, "end": v(-19.83, 25.73) * mm});
            skLineSegment(sketch, "E125", {"start": v(-11.22, 30.46) * mm, "end": v(-19.83, 30.46) * mm});
            skLineSegment(sketch, "E126", {"start": v(-19.83, 30.46) * mm, "end": v(-19.83, 25.73) * mm});
            skLineSegment(sketch, "E127", {"start": v(-11.22, 30.46) * mm, "end": v(-6.03, 20.16) * mm});
            skLineSegment(sketch, "E128", {"start": v(-6.03, 20.16) * mm, "end": v(-6.03, 29.6) * mm});
            skLineSegment(sketch, "E129", {"start": v(-6.03, 29.6) * mm, "end": v(7, 29.6) * mm});
            skLineSegment(sketch, "E130", {"start": v(7, 29.6) * mm, "end": v(13.53, 14.45) * mm});
            skLineSegment(sketch, "E131", {"start": v(13.53, 14.45) * mm, "end": v(19.45, 26.04) * mm});
            skLineSegment(sketch, "E132", {"start": v(19.45, 26.04) * mm, "end": v(21.87, 23.98) * mm});
            skLineSegment(sketch, "E133", {"start": v(21.87, 23.98) * mm, "end": v(12.1, 4.87) * mm});
            skLineSegment(sketch, "E134", {"start": v(3.67, -5.34) * mm, "end": v(1.51, -9.56) * mm});
            skFitSpline(sketch, "E135", {"points": [v(1.51, -9.56) * mm, v(1.1, -9.98) * mm, v(0.5, -10.5) * mm, v(-0.28, -10.96) * mm, v(-1.02, -11.28) * mm, v(-1.89, -11.42) * mm, v(-3.04, -11.54) * mm], "startDerivative": vector(-2.89, -2.94) * mm, "endDerivative": vector(-6.1, -0.61) * mm});
            skLineSegment(sketch, "E136", {"start": v(-3.04, -11.54) * mm, "end": v(-16.05, -12.87) * mm});
            skFitSpline(sketch, "E137", {"points": [v(-16.05, -12.87) * mm, v(-16.19, -13.4) * mm, v(-16.22, -14.3) * mm, v(-16.21, -15.34) * mm, v(-16.16, -16.3) * mm, v(-16.05, -17.12) * mm, v(-15.78, -18.27) * mm, v(-15.57, -19.1) * mm, v(-15.38, -19.55) * mm, v(-15.17, -19.8) * mm, v(-14.88, -19.93) * mm, v(-13.35, -19.65) * mm], "startDerivative": vector(-2.14, -6.44) * mm, "endDerivative": vector(14.23, 3.58) * mm});
            skLineSegment(sketch, "E138", {"start": v(6.23, -6.64) * mm, "end": v(1.64, -15.64) * mm});
            skFitSpline(sketch, "E139", {"points": [v(1.64, -15.64) * mm, v(0.93, -16.5) * mm, v(0.09, -17.15) * mm, v(-0.8, -17.46) * mm, v(-2.21, -17.74) * mm, v(-3.81, -18.02) * mm], "startDerivative": vector(-3.55, -4.67) * mm, "endDerivative": vector(-6.96, -1.2) * mm});
            skLineSegment(sketch, "E140", {"start": v(-13.35, -19.65) * mm, "end": v(-12.24, -15.7) * mm});
            skLineSegment(sketch, "E141", {"start": v(-12.24, -15.7) * mm, "end": v(-8.87, -16.72) * mm});
            skLineSegment(sketch, "E142", {"start": v(-8.87, -16.72) * mm, "end": v(-8.64, -18.84) * mm});
            skLineSegment(sketch, "E143", {"start": v(-8.64, -18.84) * mm, "end": v(-7.16, -18.59) * mm});
            skLineSegment(sketch, "E144", {"start": v(-7.16, -18.59) * mm, "end": v(-7.16, -16.99) * mm});
            skLineSegment(sketch, "E145", {"start": v(-7.16, -16.99) * mm, "end": v(-3.96, -17.62) * mm});
            skLineSegment(sketch, "E146", {"start": v(-3.96, -17.62) * mm, "end": v(-3.81, -18.02) * mm});
            skLineSegment(sketch, "E147", {"start": v(8.69, 4.87) * mm, "end": v(8.84, 4.87) * mm});
            skLineSegment(sketch, "E148", {"start": v(8.84, 4.87) * mm, "end": v(3.67, -5.34) * mm});
            skLineSegment(sketch, "E149", {"start": v(12.1, 4.87) * mm, "end": v(11.82, 4.87) * mm});
            skLineSegment(sketch, "E150", {"start": v(11.82, 4.87) * mm, "end": v(6.23, -6.64) * mm});
            skLineSegment(sketch, "E151", {"start": v(4.33, -4.32) * mm, "end": v(2.81, -7.3) * mm, "construction": true});
            skLineSegment(sketch, "E152", {"start": v(4.33, -4.32) * mm, "end": v(6.6, -5.48) * mm, "construction": true});
            skLineSegment(sketch, "E153", {"start": v(6.6, -5.48) * mm, "end": v(5.17, -8.32) * mm, "construction": true});
            skLineSegment(sketch, "E154", {"start": v(4.26, -4.5) * mm, "end": v(6.54, -5.61) * mm});
            skLineSegment(sketch, "E155", {"start": v(6.54, -5.61) * mm, "end": v(6.32, -6.04) * mm});
            skLineSegment(sketch, "E156", {"start": v(6.32, -6.04) * mm, "end": v(4.05, -4.86) * mm});
            skLineSegment(sketch, "E157", {"start": v(4.05, -4.86) * mm, "end": v(4.24, -4.49) * mm});
            skLineSegment(sketch, "E158", {"start": v(4.24, -4.49) * mm, "end": v(4.26, -4.5) * mm});
            skLineSegment(sketch, "E159", {"start": v(3.7, -5.54) * mm, "end": v(3.51, -5.93) * mm});
            skLineSegment(sketch, "E160", {"start": v(3.51, -5.93) * mm, "end": v(5.78, -7.1) * mm});
            skLineSegment(sketch, "E161", {"start": v(5.78, -7.1) * mm, "end": v(5.99, -6.7) * mm});
            skLineSegment(sketch, "E162", {"start": v(5.99, -6.7) * mm, "end": v(3.7, -5.54) * mm});
            skLineSegment(sketch, "E163", {"start": v(3.13, -6.67) * mm, "end": v(2.91, -7.11) * mm});
            skLineSegment(sketch, "E164", {"start": v(2.91, -7.11) * mm, "end": v(5.2, -8.23) * mm});
            skLineSegment(sketch, "E165", {"start": v(5.2, -8.23) * mm, "end": v(5.4, -7.87) * mm});
            skLineSegment(sketch, "E166", {"start": v(5.4, -7.87) * mm, "end": v(3.13, -6.67) * mm});
            skSolve(sketch);
        }
        {
            var Q0;
            Q0 = qSketchRegion(id + "F6", true);
            extrude(context, id + "F7", {"entities" : qUnion([Q0]), "operationType" : NewBodyOperationType.REMOVE, "oppositeDirection" : true, "depth" : 7 * mm, "offsetDistance" : 25 * mm});
        }
        {
            var Q0;
            Q0=makeQuery(id+"F1.opExtrude","CAP_EDGE",EDGE,{"disambiguationData":[OSD([sQuery(id+"F0.wireOp",EDGE,"E0")])],"isStart":false});
            fillet(context, id + "F8", {"entities" : qUnion([Q0]), "radius" : 1 * mm, "tangentPropagation" : true, "allowEdgeOverflow" : false});
        }
        {
            var Q0;
            Q0=makeQuery(id+"F1.opExtrude","CAP_FACE",FACE,{"disambiguationData":[OSD([sQuery(id+"F0.wireOp",EDGE,"E0")])],"isStart":true});
            fillet(context, id + "F9", {"entities" : qUnion([Q0]), "radius" : 1 * mm, "tangentPropagation" : true, "allowEdgeOverflow" : false});
        }
    });
